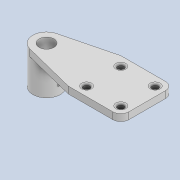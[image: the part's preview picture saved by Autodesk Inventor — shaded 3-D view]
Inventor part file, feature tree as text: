
AUTODESK INVENTOR PART (.ipt)
format: ipt  version: 2022 (Build 260153000, 153)  size: 152,576 bytes
history: native  units: in
note: dims shown in document units (in); Inventor stores cm internally (conversion verified against a paired STEP export)
features: extrude x3, sketch x3, fillet x1, chamfer x1
ambient origin geometry x8: Origin, YZ Plane, XZ Plane, XY Plane, X Axis, Y Axis, Z Axis, Center Point
bodies: Solid1 (feature_tree)
feature tree (8):
  extrude  "Extrusion1"  Depth=0.4724in
  extrude  "Extrusion2"  Depth=0.5315in
  fillet  "Fillet1"  Radius=0.5906in
  extrude  "Extrusion3"  Depth=0.0787in
  chamfer  "Chamfer1"  Distance=0.1102in
  sketch  "Sketch1"  dims[d0=0.2559in d1=0.4724in]
  sketch  "Sketch2"  dims[d2=0.5315in d3=0.0in d4=0.9843in d5=0.5906in]
  sketch  "Sketch3"  dims[d6=0.5906in d7=0.2953in d8=0.1102in d9=0.1102in d10=0.1102in d11=0.1102in d12=0.4961in d13=0.1575in d14=0.1378in d15=0.1181in d16=0.0in d17=0.0315in d18=0.0394in d19=0.0394in d20=0.3937in d21=0.3937in d22=0.0in d23=0.3937in d24=0.0787in d25=45.0deg]
